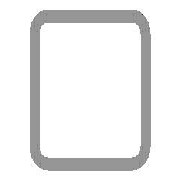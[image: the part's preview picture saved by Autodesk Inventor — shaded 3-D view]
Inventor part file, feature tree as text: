
AUTODESK INVENTOR PART (.ipt)
format: ipt  version: 2025 (Build 290162010, 162A)  size: 134,144 bytes
history: native  units: mm (DEFAULTED — no unit token found)
features: other x4, sketch x1, plane x1
ambient origin geometry x8: Origin, YZ Plane, XZ Plane, XY Plane, X Axis, Y Axis, Z Axis, Center Point
bodies: Solid1 (feature_tree), Body (feature_tree)
feature tree (6):
  parser-record x1  (decoder bookkeeping rows leaked as tree rows — omitted from the tree; the rows remain in map.json)
  other  "Driven Length"
  other  "Start Plane"
  other  "End Plane"
  sketch  "Sketch3"  dims[d3=2700.0mm d4=0.0mm d7=6.0mm d9=100.0mm d11=100.0mm d12=3.0mm d13=-0.0mm d14=2700.0mm d15=50.0mm d16=50.0mm d17=90.0deg d18=2700.0mm]
  plane  "Work Plane3"
